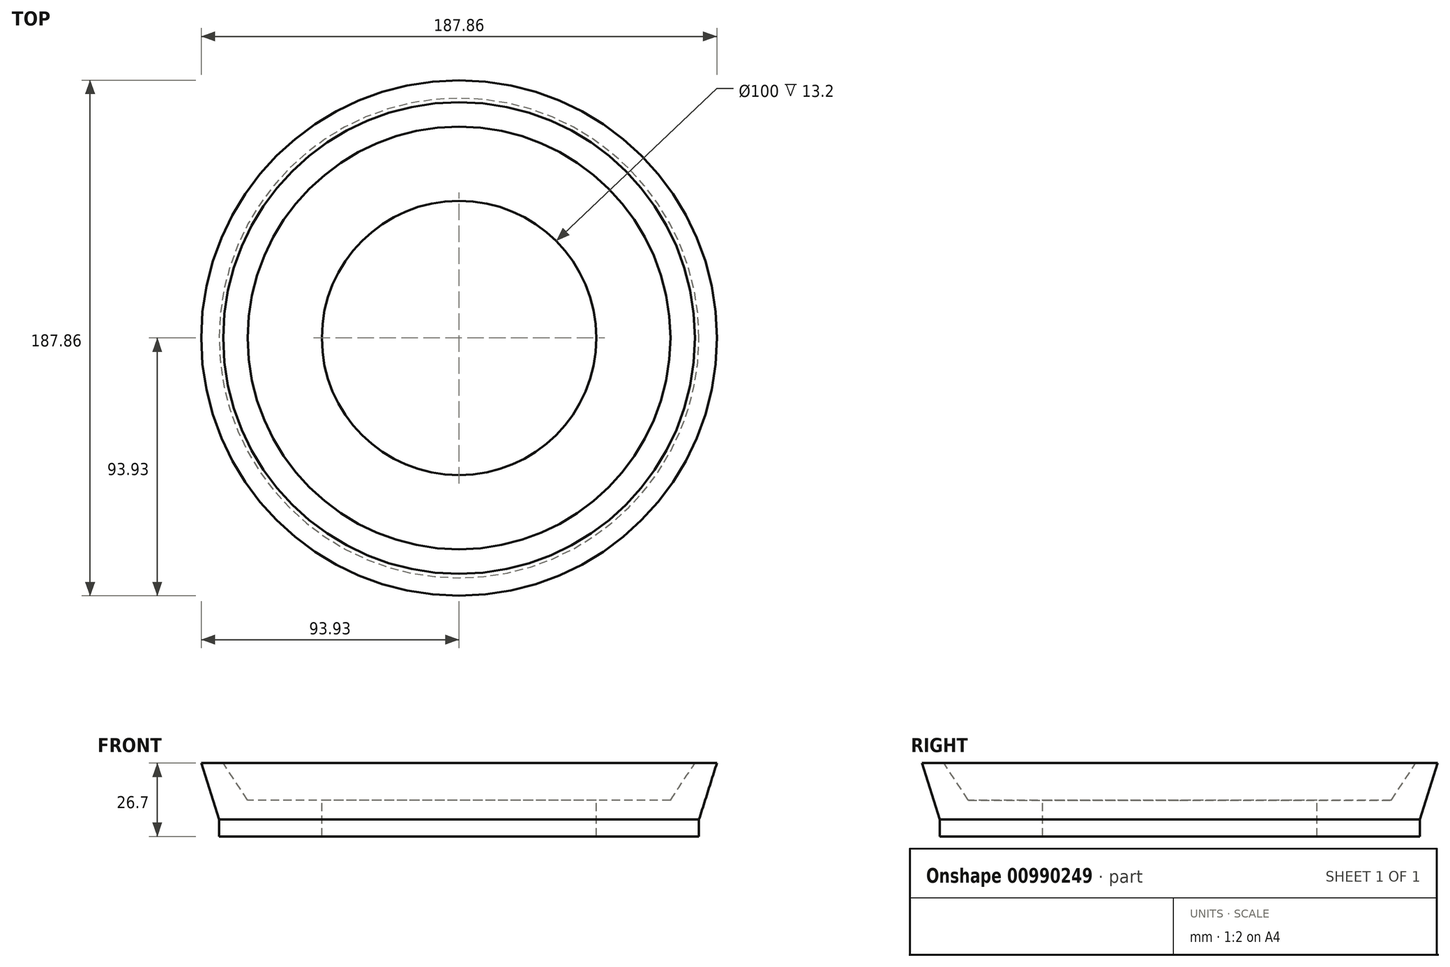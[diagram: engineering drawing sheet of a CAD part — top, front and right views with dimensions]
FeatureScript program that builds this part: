
annotation { "Feature Type Name" : "Feature", "Feature Type Description" : "" }
export const myFeature = defineFeature(function(context is Context, id is Id, definition is map)
    precondition{}
    {
        {
            var Q0;
            Q0=qCreatedBy(makeId("Front.planeOp"),FACE);
            var sketch = newSketch(context, id + "F0", { "sketchPlane" : qUnion([Q0])});
            skLineSegment(sketch, "E0", {"start": v(-87.4, 6.2) * mm, "end": v(-87.4, 0) * mm});
            skLineSegment(sketch, "E1", {"start": v(-87.4, 6.2) * mm, "end": v(-93.93, 26.7) * mm});
            skLineSegment(sketch, "E2", {"start": v(-77, 13.2) * mm, "end": v(-50, 13.2) * mm});
            skLineSegment(sketch, "E3", {"start": v(-50, 13.2) * mm, "end": v(-50, 0) * mm});
            skLineSegment(sketch, "E4", {"start": v(-50, 0) * mm, "end": v(-87.4, 0) * mm});
            skLineSegment(sketch, "E5", {"start": v(-93.93, 26.7) * mm, "end": v(-85.93, 26.7) * mm});
            skLineSegment(sketch, "E6", {"start": v(-85.93, 26.7) * mm, "end": v(-77, 13.2) * mm});
            skLineSegment(sketch, "E7", {"start": v(0, 37.44) * mm, "end": v(0, -28.16) * mm});
            skLineSegment(sketch, "E8", {"start": v(-65.4, 19.57) * mm, "end": v(-65.4, -7.5) * mm, "construction": true});
            skSolve(sketch);
        }
        {
            var Q0;
            Q0=makeQuery(id+"F0.imprint","IMPRINT",FACE,{"disambiguationData":[TD([[makeQuery(id+"F0.imprint","IMPRINT",EDGE,{"derivedFrom":sQuery(id+"F0.wireOp",EDGE,"E0")}),1.0]])]});
            var Q1;
            Q1=sQuery(id+"F0.wireOp",EDGE,"E7");
            revolve(context, id + "F1", {"surfaceOperationType" : NewSurfaceOperationType.NEW, "entities" : qUnion([Q0]), "axis" : qUnion([Q1]), "revolveType" : RevolveType.FULL});
        }
    });
